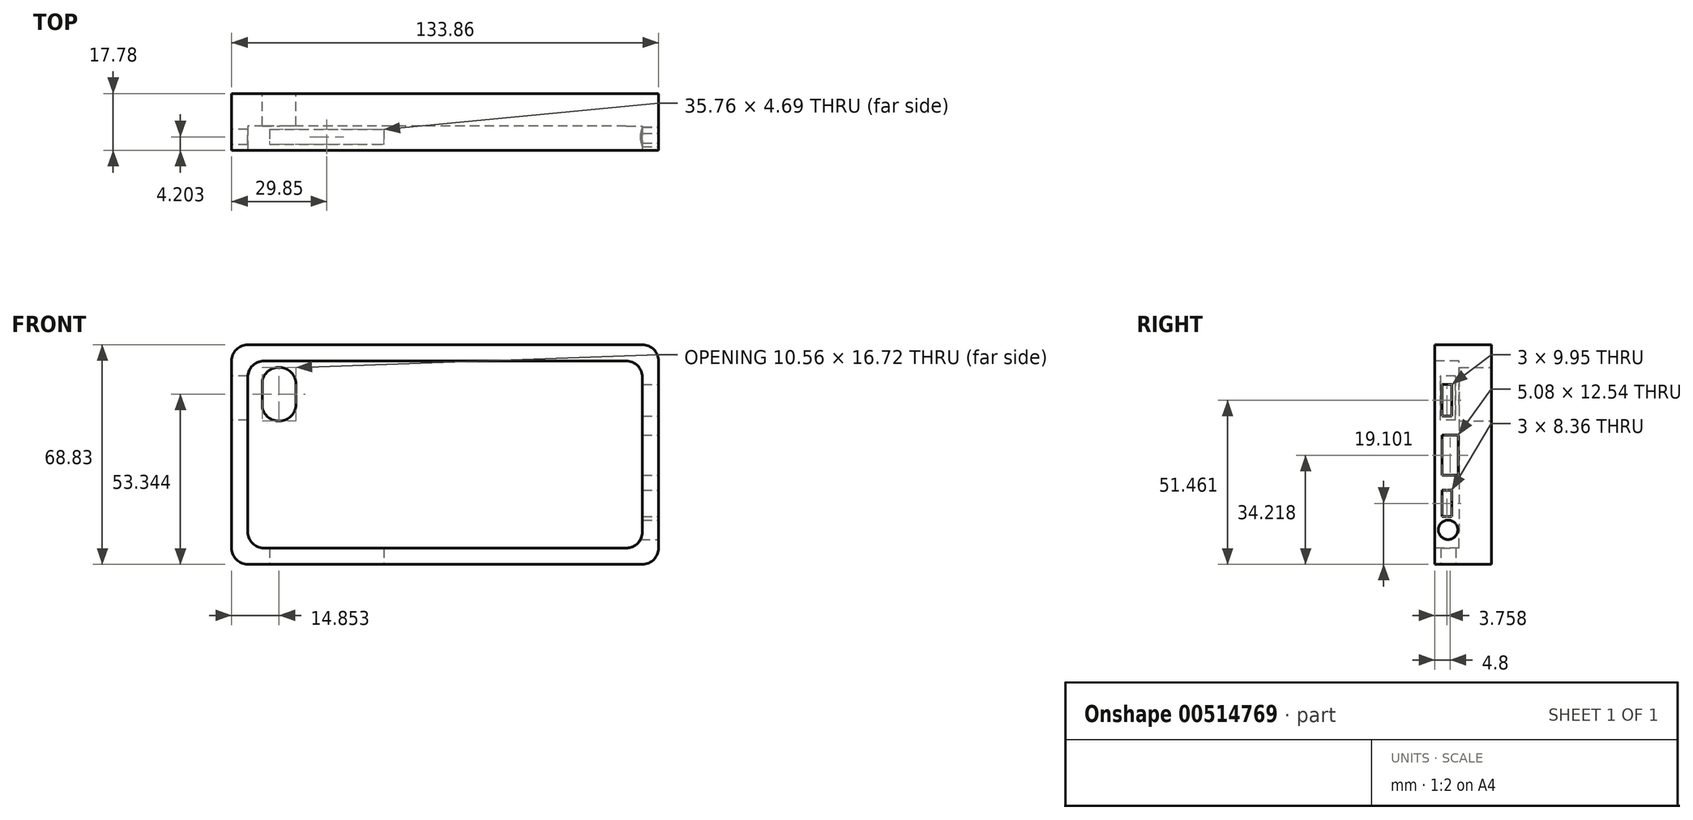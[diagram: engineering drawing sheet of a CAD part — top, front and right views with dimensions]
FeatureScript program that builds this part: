
annotation { "Feature Type Name" : "Feature", "Feature Type Description" : "" }
export const myFeature = defineFeature(function(context is Context, id is Id, definition is map)
    precondition{}
    {
        {
            var Q0;
            Q0=qCreatedBy(makeId("Front.planeOp"),FACE);
            var sketch = newSketch(context, id + "F0", { "sketchPlane" : qUnion([Q0])});
            skLineSegment(sketch, "E0", {"start": v(69.4, 0) * mm, "end": v(-64.46, 0) * mm});
            skLineSegment(sketch, "E1", {"start": v(-64.46, 0) * mm, "end": v(-64.46, 68.83) * mm});
            skLineSegment(sketch, "E2", {"start": v(-64.46, 68.83) * mm, "end": v(69.4, 68.83) * mm});
            skLineSegment(sketch, "E3", {"start": v(69.4, 68.83) * mm, "end": v(69.4, 0) * mm});
            skSolve(sketch);
        }
        {
            var Q0;
            Q0=makeQuery(id+"F0.imprint","IMPRINT",FACE,{"disambiguationData":[TD([[makeQuery(id+"F0.imprint","IMPRINT",EDGE,{"derivedFrom":sQuery(id+"F0.wireOp",EDGE,"E0")}),-1.0]])]});
            extrude(context, id + "F1", {"entities" : qUnion([Q0]), "depth" : 17.78 * mm, "offsetDistance" : 25.4 * mm});
        }
        {
            var Q0;
            Q0=makeQuery(id+"F1.opExtrude","SWEPT_EDGE",EDGE,{"disambiguationData":[OSD([sQuery(id+"F0.wireOp",EDGE,"E1"),sQuery(id+"F0.wireOp",EDGE,"E2")])]});
            var Q1;
            Q1=makeQuery(id+"F1.opExtrude","SWEPT_EDGE",EDGE,{"disambiguationData":[OSD([sQuery(id+"F0.wireOp",EDGE,"E2"),sQuery(id+"F0.wireOp",EDGE,"E3")])]});
            var Q2;
            Q2=makeQuery(id+"F1.opExtrude","SWEPT_EDGE",EDGE,{"disambiguationData":[OSD([sQuery(id+"F0.wireOp",EDGE,"E0"),sQuery(id+"F0.wireOp",EDGE,"E3")])]});
            var Q3;
            Q3=makeQuery(id+"F1.opExtrude","SWEPT_EDGE",EDGE,{"disambiguationData":[OSD([sQuery(id+"F0.wireOp",EDGE,"E0"),sQuery(id+"F0.wireOp",EDGE,"E1")])]});
            fillet(context, id + "F2", {"entities" : qUnion([Q0, Q1, Q2, Q3]), "radius" : 5.08 * mm, "tangentPropagation" : true, "allowEdgeOverflow" : false});
        }
        {
            var Q0;
            Q0=makeQuery(id+"F1.opExtrude","CAP_FACE",FACE,{"disambiguationData":[OSD([sQuery(id+"F0.wireOp",EDGE,"E0"),sQuery(id+"F0.wireOp",EDGE,"E1"),sQuery(id+"F0.wireOp",EDGE,"E2"),sQuery(id+"F0.wireOp",EDGE,"E3")])],"isStart":false});
            var sketch = newSketch(context, id + "F3", { "sketchPlane" : qUnion([Q0])});
            skLineSegment(sketch, "E4", {"start": v(-59.38, 63.75) * mm, "end": v(64.32, 63.75) * mm});
            skLineSegment(sketch, "E5", {"start": v(64.32, 63.75) * mm, "end": v(64.32, 5.08) * mm});
            skLineSegment(sketch, "E6", {"start": v(64.32, 5.08) * mm, "end": v(-59.38, 5.08) * mm});
            skLineSegment(sketch, "E7", {"start": v(-59.38, 5.08) * mm, "end": v(-59.38, 63.75) * mm});
            skSolve(sketch);
        }
        {
            var Q0;
            Q0 = qSketchRegion(id + "F3", true);
            extrude(context, id + "F4", {"entities" : qUnion([Q0]), "operationType" : NewBodyOperationType.REMOVE, "oppositeDirection" : true, "depth" : 7.62 * mm, "offsetDistance" : 25.4 * mm});
        }
        {
            var Q0;
            Q0=makeQuery(id+"F4.boolean.opBoolean","COPY",EDGE,{"derivedFrom":makeQuery(id+"F4.opExtrude","SWEPT_EDGE",EDGE,{"disambiguationData":[OSD([sQuery(id+"F3.wireOp",EDGE,"E4"),sQuery(id+"F3.wireOp",EDGE,"E7")])]})});
            var Q1;
            Q1=makeQuery(id+"F4.boolean.opBoolean","COPY",EDGE,{"derivedFrom":makeQuery(id+"F4.opExtrude","SWEPT_EDGE",EDGE,{"disambiguationData":[OSD([sQuery(id+"F3.wireOp",EDGE,"E6"),sQuery(id+"F3.wireOp",EDGE,"E7")])]})});
            var Q2;
            Q2=makeQuery(id+"F4.boolean.opBoolean","COPY",EDGE,{"derivedFrom":makeQuery(id+"F4.opExtrude","SWEPT_EDGE",EDGE,{"disambiguationData":[OSD([sQuery(id+"F3.wireOp",EDGE,"E4"),sQuery(id+"F3.wireOp",EDGE,"E5")])]})});
            var Q3;
            Q3=makeQuery(id+"F4.boolean.opBoolean","COPY",EDGE,{"derivedFrom":makeQuery(id+"F4.opExtrude","SWEPT_EDGE",EDGE,{"disambiguationData":[OSD([sQuery(id+"F3.wireOp",EDGE,"E5"),sQuery(id+"F3.wireOp",EDGE,"E6")])]})});
            fillet(context, id + "F5", {"entities" : qUnion([Q0, Q1, Q2, Q3]), "radius" : 5.08 * mm, "tangentPropagation" : true, "allowEdgeOverflow" : false});
        }
        {
            var Q0;
            Q0=makeQuery(id+"F1.opExtrude","SWEPT_FACE",FACE,{"disambiguationData":[OSD([sQuery(id+"F0.wireOp",EDGE,"E3")])]});
            var sketch = newSketch(context, id + "F6", { "sketchPlane" : qUnion([Q0])});
            skCircle(sketch, "E8", {"center": v(-13.61, 10.81) * mm, "radius": 3.04 * mm});
            skLineSegment(sketch, "E9.bottom", {"start": v(-12.52, 14.92) * mm, "end": v(-15.52, 14.92) * mm});
            skLineSegment(sketch, "E9.top", {"start": v(-12.52, 23.28) * mm, "end": v(-15.52, 23.28) * mm});
            skLineSegment(sketch, "E9.left", {"start": v(-12.52, 14.92) * mm, "end": v(-12.52, 23.28) * mm});
            skLineSegment(sketch, "E9.right", {"start": v(-15.52, 14.92) * mm, "end": v(-15.52, 23.28) * mm});
            skPoint(sketch, "E10.oppositeSnap0", {"position": v(-15.52, 19.1) * mm});
            skLineSegment(sketch, "E10.bottom", {"start": v(-10.44, 27.95) * mm, "end": v(-15.52, 27.95) * mm});
            skLineSegment(sketch, "E10.top", {"start": v(-10.44, 40.49) * mm, "end": v(-15.52, 40.49) * mm});
            skLineSegment(sketch, "E10.left", {"start": v(-10.44, 27.95) * mm, "end": v(-10.44, 40.49) * mm});
            skLineSegment(sketch, "E10.right", {"start": v(-15.52, 27.95) * mm, "end": v(-15.52, 40.49) * mm});
            skLineSegment(sketch, "E11.bottom", {"start": v(-12.52, 46.48) * mm, "end": v(-15.52, 46.48) * mm});
            skLineSegment(sketch, "E11.top", {"start": v(-12.52, 56.44) * mm, "end": v(-15.52, 56.44) * mm});
            skLineSegment(sketch, "E11.left", {"start": v(-12.52, 46.48) * mm, "end": v(-12.52, 56.44) * mm});
            skLineSegment(sketch, "E11.right", {"start": v(-15.52, 46.48) * mm, "end": v(-15.52, 56.44) * mm});
            skSolve(sketch);
        }
        {
            var Q0;
            Q0 = qSketchRegion(id + "F6", true);
            extrude(context, id + "F7", {"entities" : qUnion([Q0]), "operationType" : NewBodyOperationType.REMOVE, "oppositeDirection" : true, "depth" : 25.4 * mm, "offsetDistance" : 25.4 * mm});
        }
        {
            var Q0;
            Q0=makeQuery(id+"F1.opExtrude","SWEPT_FACE",FACE,{"disambiguationData":[OSD([sQuery(id+"F0.wireOp",EDGE,"E0")])]});
            var sketch = newSketch(context, id + "F8", { "sketchPlane" : qUnion([Q0])});
            skLineSegment(sketch, "E12.bottom", {"start": v(-52.49, 11.23) * mm, "end": v(-16.73, 11.23) * mm});
            skLineSegment(sketch, "E12.top", {"start": v(-52.49, 15.92) * mm, "end": v(-16.73, 15.92) * mm});
            skLineSegment(sketch, "E12.left", {"start": v(-52.49, 11.23) * mm, "end": v(-52.49, 15.92) * mm});
            skLineSegment(sketch, "E12.right", {"start": v(-16.73, 11.23) * mm, "end": v(-16.73, 15.92) * mm});
            skSolve(sketch);
        }
        {
            var Q0;
            Q0 = qSketchRegion(id + "F8", true);
            extrude(context, id + "F9", {"entities" : qUnion([Q0]), "operationType" : NewBodyOperationType.REMOVE, "oppositeDirection" : true, "depth" : 25.4 * mm, "offsetDistance" : 25.4 * mm});
        }
        {
            var Q0;
            Q0=makeQuery(id+"F1.opExtrude","SWEPT_FACE",FACE,{"disambiguationData":[OSD([sQuery(id+"F0.wireOp",EDGE,"E1")])]});
            var sketch = newSketch(context, id + "F10", { "sketchPlane" : qUnion([Q0])});
            skLineSegment(sketch, "E13.bottom", {"start": v(11.27, 59) * mm, "end": v(16.04, 59) * mm});
            skLineSegment(sketch, "E13.top", {"start": v(11.27, 45.26) * mm, "end": v(16.04, 45.26) * mm});
            skLineSegment(sketch, "E13.left", {"start": v(11.27, 59) * mm, "end": v(11.27, 45.26) * mm});
            skLineSegment(sketch, "E13.right", {"start": v(16.04, 59) * mm, "end": v(16.04, 45.26) * mm});
            skSolve(sketch);
        }
        {
            var Q0;
            Q0=makeQuery(id+"F10.imprint","IMPRINT",FACE,{"disambiguationData":[TD([[makeQuery(id+"F10.imprint","IMPRINT",EDGE,{"derivedFrom":sQuery(id+"F10.wireOp",EDGE,"E13.bottom")}),-1.0]])]});
            extrude(context, id + "F11", {"entities" : qUnion([Q0]), "operationType" : NewBodyOperationType.REMOVE, "oppositeDirection" : true, "depth" : 25.4 * mm, "offsetDistance" : 25.4 * mm});
        }
        {
            var Q0;
            Q0=makeQuery(id+"F1.opExtrude","CAP_FACE",FACE,{"disambiguationData":[OSD([sQuery(id+"F0.wireOp",EDGE,"E0"),sQuery(id+"F0.wireOp",EDGE,"E1"),sQuery(id+"F0.wireOp",EDGE,"E2"),sQuery(id+"F0.wireOp",EDGE,"E3")])],"isStart":true});
            var sketch = newSketch(context, id + "F12", { "sketchPlane" : qUnion([Q0])});
            skLineSegment(sketch, "E14.bottom", {"start": v(44.32, 61.7) * mm, "end": v(54.89, 61.7) * mm});
            skLineSegment(sketch, "E14.top", {"start": v(44.32, 44.99) * mm, "end": v(54.89, 44.99) * mm});
            skLineSegment(sketch, "E14.left", {"start": v(44.32, 61.7) * mm, "end": v(44.32, 44.99) * mm});
            skLineSegment(sketch, "E14.right", {"start": v(54.89, 61.7) * mm, "end": v(54.89, 44.99) * mm});
            skSolve(sketch);
        }
        {
            var Q0;
            Q0=makeQuery(id+"F12.imprint","IMPRINT",FACE,{"disambiguationData":[TD([[makeQuery(id+"F12.imprint","IMPRINT",EDGE,{"derivedFrom":sQuery(id+"F12.wireOp",EDGE,"E14.bottom")}),-1.0]])]});
            extrude(context, id + "F13", {"entities" : qUnion([Q0]), "operationType" : NewBodyOperationType.REMOVE, "oppositeDirection" : true, "depth" : 25.4 * mm, "offsetDistance" : 25.4 * mm});
        }
        {
            var Q0;
            Q0=makeQuery(id+"F13.boolean.opBoolean","COPY",EDGE,{"derivedFrom":makeQuery(id+"F13.opExtrude","SWEPT_EDGE",EDGE,{"disambiguationData":[OSD([sQuery(id+"F12.wireOp",EDGE,"E14.bottom"),sQuery(id+"F12.wireOp",EDGE,"E14.right")])]})});
            var Q1;
            Q1=makeQuery(id+"F13.boolean.opBoolean","COPY",EDGE,{"derivedFrom":makeQuery(id+"F13.opExtrude","SWEPT_EDGE",EDGE,{"disambiguationData":[OSD([sQuery(id+"F12.wireOp",EDGE,"E14.top"),sQuery(id+"F12.wireOp",EDGE,"E14.right")])]})});
            var Q2;
            Q2=makeQuery(id+"F13.boolean.opBoolean","COPY",EDGE,{"derivedFrom":makeQuery(id+"F13.opExtrude","SWEPT_EDGE",EDGE,{"disambiguationData":[OSD([sQuery(id+"F12.wireOp",EDGE,"E14.top"),sQuery(id+"F12.wireOp",EDGE,"E14.left")])]})});
            var Q3;
            Q3=makeQuery(id+"F13.boolean.opBoolean","COPY",EDGE,{"derivedFrom":makeQuery(id+"F13.opExtrude","SWEPT_EDGE",EDGE,{"disambiguationData":[OSD([sQuery(id+"F12.wireOp",EDGE,"E14.bottom"),sQuery(id+"F12.wireOp",EDGE,"E14.left")])]})});
            fillet(context, id + "F14", {"entities" : qUnion([Q0, Q1, Q2, Q3]), "radius" : 5.08 * mm, "tangentPropagation" : true, "allowEdgeOverflow" : false});
        }
    });
